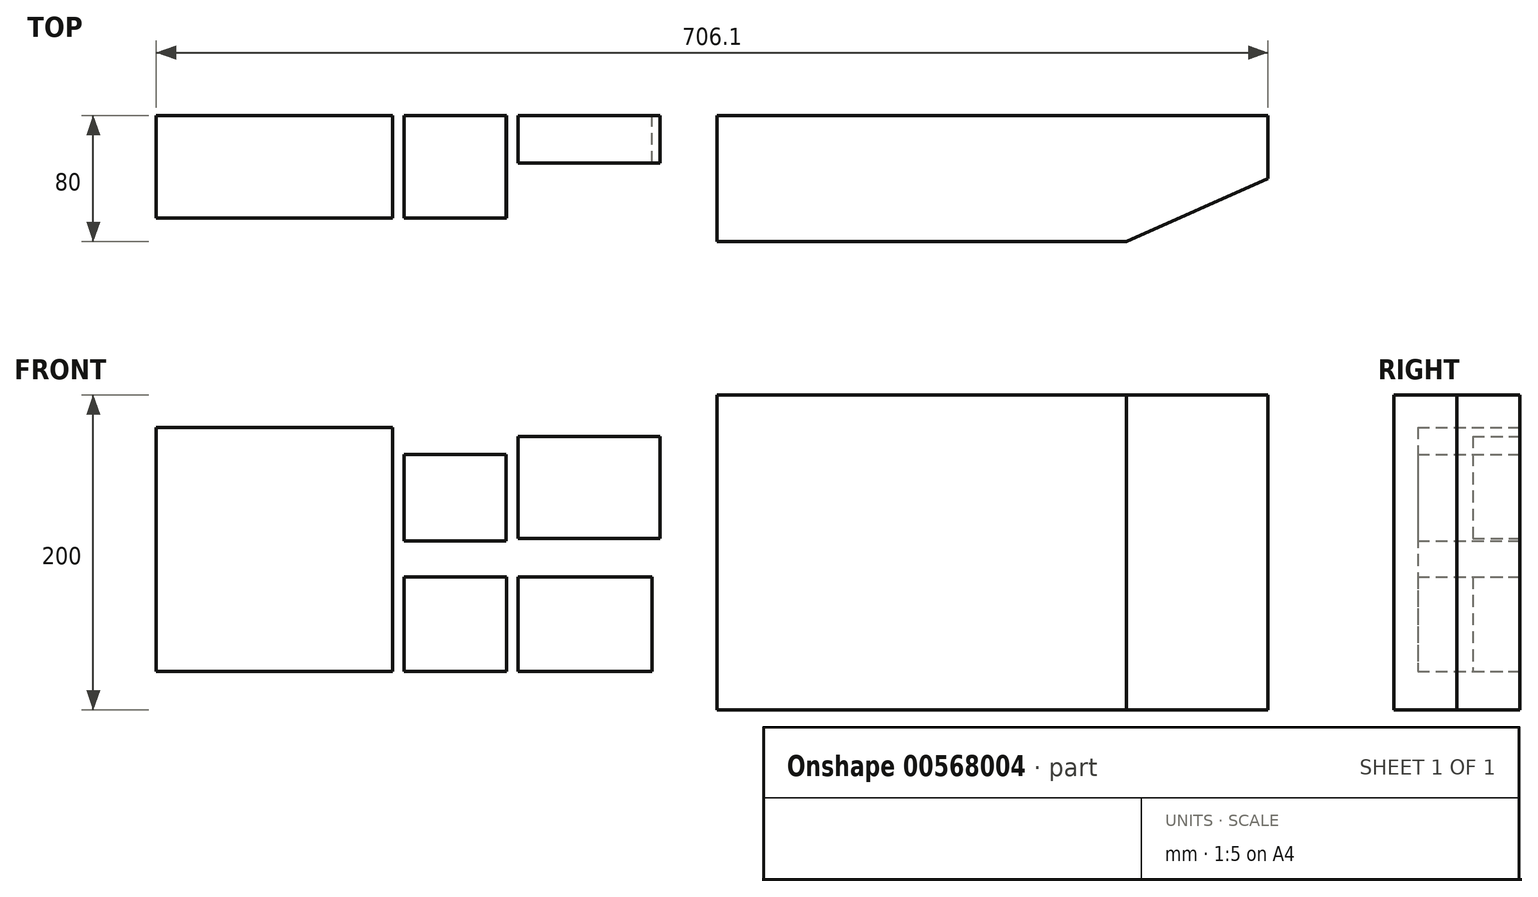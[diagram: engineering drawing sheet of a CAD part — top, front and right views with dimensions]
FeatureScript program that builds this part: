
annotation { "Feature Type Name" : "Feature", "Feature Type Description" : "" }
export const myFeature = defineFeature(function(context is Context, id is Id, definition is map)
    precondition{}
    {
        {
            var Q0;
            Q0=qCreatedBy(makeId("Front.planeOp"),FACE);
            var sketch = newSketch(context, id + "F0", { "sketchPlane" : qUnion([Q0])});
            skLineSegment(sketch, "E0.bottom", {"start": v(-59.84, 26.86) * mm, "end": v(90.16, 26.86) * mm});
            skLineSegment(sketch, "E0.top", {"start": v(-59.84, -128.14) * mm, "end": v(90.16, -128.14) * mm});
            skLineSegment(sketch, "E0.left", {"start": v(-59.84, 26.86) * mm, "end": v(-59.84, -128.14) * mm});
            skLineSegment(sketch, "E0.right", {"start": v(90.16, 26.86) * mm, "end": v(90.16, -128.14) * mm});
            skLineSegment(sketch, "E1.bottom", {"start": v(169.92, -68.14) * mm, "end": v(254.92, -68.14) * mm});
            skLineSegment(sketch, "E1.top", {"start": v(169.92, -128.14) * mm, "end": v(254.92, -128.14) * mm});
            skLineSegment(sketch, "E1.left", {"start": v(169.92, -68.14) * mm, "end": v(169.92, -128.14) * mm});
            skLineSegment(sketch, "E1.right", {"start": v(254.92, -68.14) * mm, "end": v(254.92, -128.14) * mm});
            skLineSegment(sketch, "E2.bottom", {"start": v(97.4, 9.8) * mm, "end": v(162.4, 9.8) * mm});
            skLineSegment(sketch, "E2.top", {"start": v(97.4, -45.2) * mm, "end": v(162.4, -45.2) * mm});
            skLineSegment(sketch, "E2.left", {"start": v(97.4, 9.8) * mm, "end": v(97.4, -45.2) * mm});
            skLineSegment(sketch, "E2.right", {"start": v(162.4, 9.8) * mm, "end": v(162.4, -45.2) * mm});
            skLineSegment(sketch, "E3.bottom", {"start": v(97.63, -68.14) * mm, "end": v(162.63, -68.14) * mm});
            skLineSegment(sketch, "E3.top", {"start": v(97.63, -128.14) * mm, "end": v(162.63, -128.14) * mm});
            skLineSegment(sketch, "E3.left", {"start": v(97.63, -68.14) * mm, "end": v(97.63, -128.14) * mm});
            skLineSegment(sketch, "E3.right", {"start": v(162.63, -68.14) * mm, "end": v(162.63, -128.14) * mm});
            skLineSegment(sketch, "E4.bottom", {"start": v(169.92, 21.2) * mm, "end": v(259.92, 21.2) * mm});
            skLineSegment(sketch, "E4.top", {"start": v(169.92, -43.8) * mm, "end": v(259.92, -43.8) * mm});
            skLineSegment(sketch, "E4.left", {"start": v(169.92, 21.2) * mm, "end": v(169.92, -43.8) * mm});
            skLineSegment(sketch, "E4.right", {"start": v(259.92, 21.2) * mm, "end": v(259.92, -43.8) * mm});
            skLineSegment(sketch, "E5.bottom", {"start": v(296.26, 47.42) * mm, "end": v(646.26, 47.42) * mm});
            skLineSegment(sketch, "E5.top", {"start": v(296.26, -152.58) * mm, "end": v(646.26, -152.58) * mm});
            skLineSegment(sketch, "E5.left", {"start": v(646.26, 47.42) * mm, "end": v(646.26, -152.58) * mm});
            skLineSegment(sketch, "E5.right", {"start": v(296.26, 47.42) * mm, "end": v(296.26, -152.58) * mm});
            skLineSegment(sketch, "E6", {"start": v(556.26, -152.58) * mm, "end": v(556.26, 47.42) * mm});
            skSolve(sketch);
        }
        {
            var Q0;
            Q0=makeQuery(id+"F0.imprint","IMPRINT",FACE,{"disambiguationData":[TD([[makeQuery(id+"F0.imprint","IMPRINT",EDGE,{"derivedFrom":sQuery(id+"F0.wireOp",EDGE,"E0.bottom")}),-1.0]])]});
            var Q1;
            Q1=makeQuery(id+"F0.imprint","IMPRINT",FACE,{"disambiguationData":[TD([[makeQuery(id+"F0.imprint","IMPRINT",EDGE,{"derivedFrom":sQuery(id+"F0.wireOp",EDGE,"E3.bottom")}),-1.0]])]});
            var Q2;
            Q2=makeQuery(id+"F0.imprint","IMPRINT",FACE,{"disambiguationData":[TD([[makeQuery(id+"F0.imprint","IMPRINT",EDGE,{"derivedFrom":sQuery(id+"F0.wireOp",EDGE,"E2.bottom")}),-1.0]])]});
            extrude(context, id + "F1", {"entities" : qUnion([Q0, Q1, Q2]), "depth" : 65 * mm, "offsetDistance" : 25 * mm});
        }
        {
            var Q0;
            {var subQ0=sQuery(id+"F0.wireOp",EDGE,"E5.right");Q0=makeQuery(id+"F0.imprint","IMPRINT",FACE,{"disambiguationData":[TD([[makeQuery(id+"F0.imprint","IMPRINT",EDGE,{"derivedFrom":subQ0}),1.0]])]});}
            extrude(context, id + "F2", {"entities" : qUnion([Q0]), "depth" : 80 * mm, "offsetDistance" : 25 * mm});
        }
        {
            var Q0;
            {var subQ0=sQuery(id+"F0.wireOp",EDGE,"E5.left");Q0=makeQuery(id+"F0.imprint","IMPRINT",FACE,{"disambiguationData":[TD([[makeQuery(id+"F0.imprint","IMPRINT",EDGE,{"derivedFrom":subQ0}),-1.0]])]});}
            extrude(context, id + "F3", {"entities" : qUnion([Q0]), "operationType" : NewBodyOperationType.ADD, "depth" : 40 * mm, "offsetDistance" : 25 * mm});
        }
        {
            var Q0;
            {var subQ0=sQuery(id+"F0.wireOp",EDGE,"E5.top");Q0=makeQuery(id+"F3.boolean.opBoolean","MERGE",FACE,{"derivedFrom":[makeQuery(id+"F2.opExtrude","SWEPT_FACE",FACE,{"disambiguationData":[OSD([subQ0])]}),makeQuery(id+"F3.opExtrude","SWEPT_FACE",FACE,{"disambiguationData":[OSD([subQ0])]})]});}
            var sketch = newSketch(context, id + "F4", { "sketchPlane" : qUnion([Q0])});
            skLineSegment(sketch, "E7", {"start": v(556.26, 80) * mm, "end": v(646.26, 40) * mm});
            skLineSegment(sketch, "E8", {"start": v(646.26, 40) * mm, "end": v(556.26, 40) * mm});
            skLineSegment(sketch, "E9", {"start": v(556.26, 40) * mm, "end": v(556.26, 80) * mm});
            skSolve(sketch);
        }
        {
            var Q0;
            Q0=makeQuery(id+"F4.imprint","IMPRINT",FACE,{"disambiguationData":[TD([[makeQuery(id+"F4.imprint","IMPRINT",EDGE,{"derivedFrom":sQuery(id+"F4.wireOp",EDGE,"E7")}),-1.0]])]});
            extrude(context, id + "F5", {"entities" : qUnion([Q0]), "operationType" : NewBodyOperationType.ADD, "oppositeDirection" : true, "depth" : 200 * mm, "offsetDistance" : 25 * mm});
        }
        {
            var Q0;
            Q0=makeQuery(id+"F0.imprint","IMPRINT",FACE,{"disambiguationData":[TD([[makeQuery(id+"F0.imprint","IMPRINT",EDGE,{"derivedFrom":sQuery(id+"F0.wireOp",EDGE,"E1.bottom")}),-1.0]])]});
            var Q1;
            Q1=makeQuery(id+"F0.imprint","IMPRINT",FACE,{"disambiguationData":[TD([[makeQuery(id+"F0.imprint","IMPRINT",EDGE,{"derivedFrom":sQuery(id+"F0.wireOp",EDGE,"E4.bottom")}),-1.0]])]});
            extrude(context, id + "F6", {"entities" : qUnion([Q0, Q1]), "depth" : 30 * mm, "offsetDistance" : 25 * mm});
        }
    });
